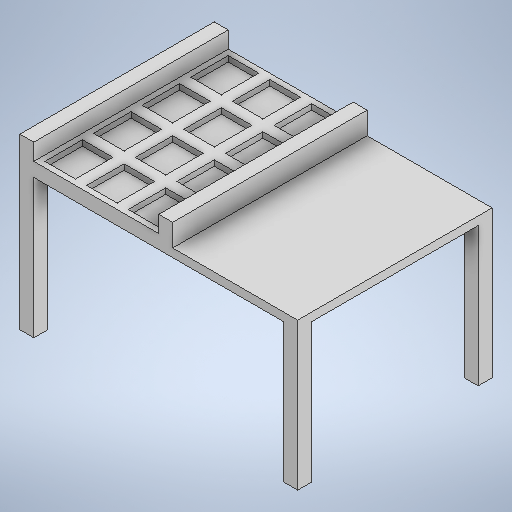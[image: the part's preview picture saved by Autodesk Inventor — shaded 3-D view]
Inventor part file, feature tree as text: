
AUTODESK INVENTOR PART (.ipt)
format: ipt  version: 2025 (Build 290162000, 162)  size: 379,392 bytes
history: native  units: in
note: dims shown in document units (in); Inventor stores cm internally (conversion verified against a paired STEP export)
features: extrude x4, sketch x3
ambient origin geometry x8: Origin, YZ Plane, XZ Plane, XY Plane, X Axis, Y Axis, Z Axis, Center Point
bodies: Solid1 (feature_tree)
feature tree (7):
  sketch  "Sketch1"  dims[d0=39.3701in d1=27.5591in]
  extrude  "Extrusion1"  Depth=27.5591in
  extrude  "Extrusion2"  Depth=1.9685in
  extrude  "Extrusion3"  Depth=4.3307in TaperAngle=0.0deg
  extrude  "Extrusion4"  Depth=1.1811in TaperAngle=0.0deg
  sketch  "Sketch2"  dims[d2=21.6535in d3=1.9685in]
  sketch  "Sketch3"  dims[d4=1.9685in d5=4.3307in d6=0.0in d7=1.1811in d8=0.0in d9=1.9685in d10=1.9685in d11=1.9685in d12=1.9685in d13=1.9685in d14=1.9685in d15=1.9685in d16=1.9685in d17=19.685in d18=0.0in d19=5.9055in d20=5.9055in d21=5.9055in d22=0.0in d23=27.5591in d24=6.8898in d25=6.8898in d26=6.8898in d27=6.8898in d28=0.7874in d29=0.7874in d30=0.7874in d31=0.7874in d32=0.7874in d33=0.7874in d34=0.7874in d35=0.7874in d36=4.3307in d37=4.3307in d38=0.7874in d39=0.7874in d40=0.7874in d41=0.7874in d42=0.7874in d43=0.7874in d44=0.7874in d45=0.7874in d46=0.7874in d47=0.7874in d48=0.7874in d49=0.7874in d50=0.7874in d51=0.0in]
